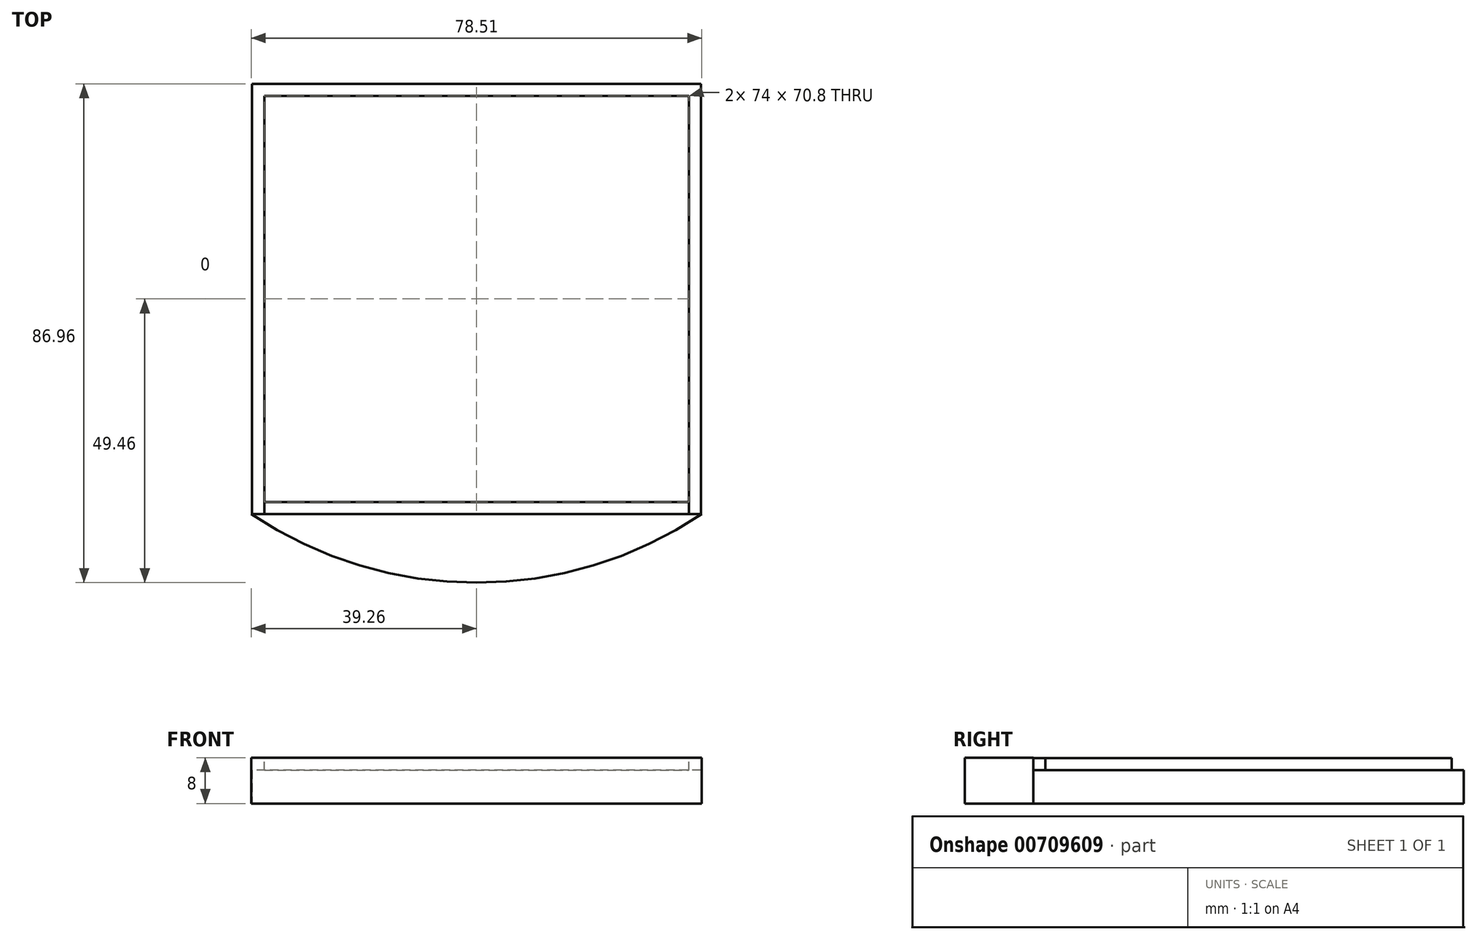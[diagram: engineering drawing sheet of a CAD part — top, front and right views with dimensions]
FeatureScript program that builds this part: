
annotation { "Feature Type Name" : "Feature", "Feature Type Description" : "" }
export const myFeature = defineFeature(function(context is Context, id is Id, definition is map)
    precondition{}
    {
        {
            var Q0;
            Q0=qCreatedBy(makeId("Top.planeOp"),FACE);
            var sketch = newSketch(context, id + "F0", { "sketchPlane" : qUnion([Q0])});
            skLineSegment(sketch, "E0", {"start": v(0, 0) * mm, "end": v(-39.1, 0) * mm});
            skLineSegment(sketch, "E1", {"start": v(-39.1, 0) * mm, "end": v(-39.1, 75) * mm});
            skLineSegment(sketch, "E2", {"start": v(-39.1, 75) * mm, "end": v(0, 75) * mm});
            skLineSegment(sketch, "E3", {"start": v(0, 75) * mm, "end": v(39.1, 75) * mm});
            skLineSegment(sketch, "E4", {"start": v(39.1, 75) * mm, "end": v(39.1, 0) * mm});
            skLineSegment(sketch, "E5", {"start": v(39.1, 0) * mm, "end": v(0, 0) * mm});
            skSolve(sketch);
        }
        {
            var Q0;
            Q0 = qSketchRegion(id + "F0", true);
            extrude(context, id + "F1", {"entities" : qUnion([Q0]), "depth" : 7.9 * mm, "offsetDistance" : 25 * mm});
        }
        {
            var Q0;
            Q0=makeQuery(id+"F1.opExtrude","CAP_FACE",FACE,{"disambiguationData":[OSD([sQuery(id+"F0.wireOp",EDGE,"E0"),sQuery(id+"F0.wireOp",EDGE,"E1"),sQuery(id+"F0.wireOp",EDGE,"E2"),sQuery(id+"F0.wireOp",EDGE,"E3"),sQuery(id+"F0.wireOp",EDGE,"E4"),sQuery(id+"F0.wireOp",EDGE,"E5")])],"isStart":false});
            var sketch = newSketch(context, id + "F2", { "sketchPlane" : qUnion([Q0])});
            skLineSegment(sketch, "E6.0", {"start": v(-37, 2.1) * mm, "end": v(37, 2.1) * mm});
            skLineSegment(sketch, "E6.1", {"start": v(-37, 72.9) * mm, "end": v(-37, 2.1) * mm});
            skLineSegment(sketch, "E6.2", {"start": v(37, 72.9) * mm, "end": v(-37, 72.9) * mm});
            skLineSegment(sketch, "E6.3", {"start": v(37, 2.1) * mm, "end": v(37, 72.9) * mm});
            skSolve(sketch);
        }
        {
            var Q0;
            Q0=makeQuery(id+"F2.imprint","IMPRINT",FACE,{"disambiguationData":[TD([[makeQuery(id+"F2.imprint","IMPRINT",EDGE,{"derivedFrom":sQuery(id+"F2.wireOp",EDGE,"E6.0")}),-1.0]])]});
            extrude(context, id + "F3", {"entities" : qUnion([Q0]), "operationType" : NewBodyOperationType.REMOVE, "oppositeDirection" : true, "depth" : 2.1 * mm, "offsetDistance" : 25 * mm});
        }
        {
            var Q0;
            Q0=makeQuery(id+"F1.opExtrude","CAP_FACE",FACE,{"disambiguationData":[OSD([sQuery(id+"F0.wireOp",EDGE,"E0"),sQuery(id+"F0.wireOp",EDGE,"E1"),sQuery(id+"F0.wireOp",EDGE,"E2"),sQuery(id+"F0.wireOp",EDGE,"E3"),sQuery(id+"F0.wireOp",EDGE,"E4"),sQuery(id+"F0.wireOp",EDGE,"E5")])],"isStart":false});
            var sketch = newSketch(context, id + "F4", { "sketchPlane" : qUnion([Q0])});
            skLineSegment(sketch, "E7", {"start": v(-37, 2.1) * mm, "end": v(-37, 0) * mm});
            skLineSegment(sketch, "E8", {"start": v(-37, 0) * mm, "end": v(37, 0) * mm});
            skLineSegment(sketch, "E9", {"start": v(37, 0) * mm, "end": v(37, 2.1) * mm});
            skLineSegment(sketch, "E10", {"start": v(37, 2.1) * mm, "end": v(-37, 2.1) * mm});
            skSolve(sketch);
        }
        {
            var Q0;
            Q0=makeQuery(id+"F4.imprint","IMPRINT",FACE,{"disambiguationData":[TD([[makeQuery(id+"F4.imprint","IMPRINT",EDGE,{"derivedFrom":sQuery(id+"F4.wireOp",EDGE,"E7")}),1.0]])]});
            extrude(context, id + "F5", {"entities" : qUnion([Q0]), "oppositeDirection" : true, "depth" : 2.1 * mm, "offsetDistance" : 25 * mm});
        }
        {
            var Q0;
            Q0=qCreatedBy(makeId("Top.planeOp"),FACE);
            var sketch = newSketch(context, id + "F6", { "sketchPlane" : qUnion([Q0])});
            skLineSegment(sketch, "E11", {"start": v(0, 96.04) * mm, "end": v(0, -11.96) * mm});
            skArc(sketch, "E12", {"start": v(-39.26, 0) * mm, "mid": v(0, -11.96) * mm, "end": v(39.25, 0) * mm});
            skLineSegment(sketch, "E13", {"start": v(-39.26, 0) * mm, "end": v(39.25, 0) * mm});
            skSolve(sketch);
        }
        {
            var Q0;
            Q0 = qSketchRegion(id + "F6", true);
            extrude(context, id + "F7", {"entities" : qUnion([Q0]), "depth" : 8 * mm, "offsetDistance" : 25 * mm});
        }
    });
